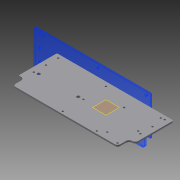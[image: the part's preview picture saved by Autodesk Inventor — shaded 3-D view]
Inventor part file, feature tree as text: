
AUTODESK INVENTOR PART (.ipt)
format: ipt  version: 2015 (Build 190159000, 159)  size: 246,784 bytes
history: native  units: mm
features: reference x11, plane x2, extrude x2, sketch x2, projected_geometry x1
ambient origin geometry x8: Origin, YZ Plane, XZ Plane, XY Plane, X Axis, Y Axis, Z Axis, Center Point
bodies: Body1 (feature_tree)
feature tree (18):
  plane  "Work Plane1"
  plane  "Work Plane2"
  extrude  "Extrusion3"  Depth=2.5mm
  extrude  "Extrusion6"  Depth=5.0mm
  sketch  "Sketch3"  dims[d20=2.5mm d21=0.0mm d26=1.0mm]
  reference  "Reference22"
  sketch  "Sketch5"  dims[d30=10.0mm d31=0.0mm d32=1.0mm d33=80.0mm d35=5.0mm]
  reference  "Reference25"
  reference  "Reference26"
  projected_geometry  "Projected Loop2"
  reference  "Reference27"
  reference  "Reference28"
  reference  "Reference29"
  reference  "Reference30"
  reference  "Reference31"
  reference  "Reference32"
  reference  "Reference33"
  reference  "Reference34"
